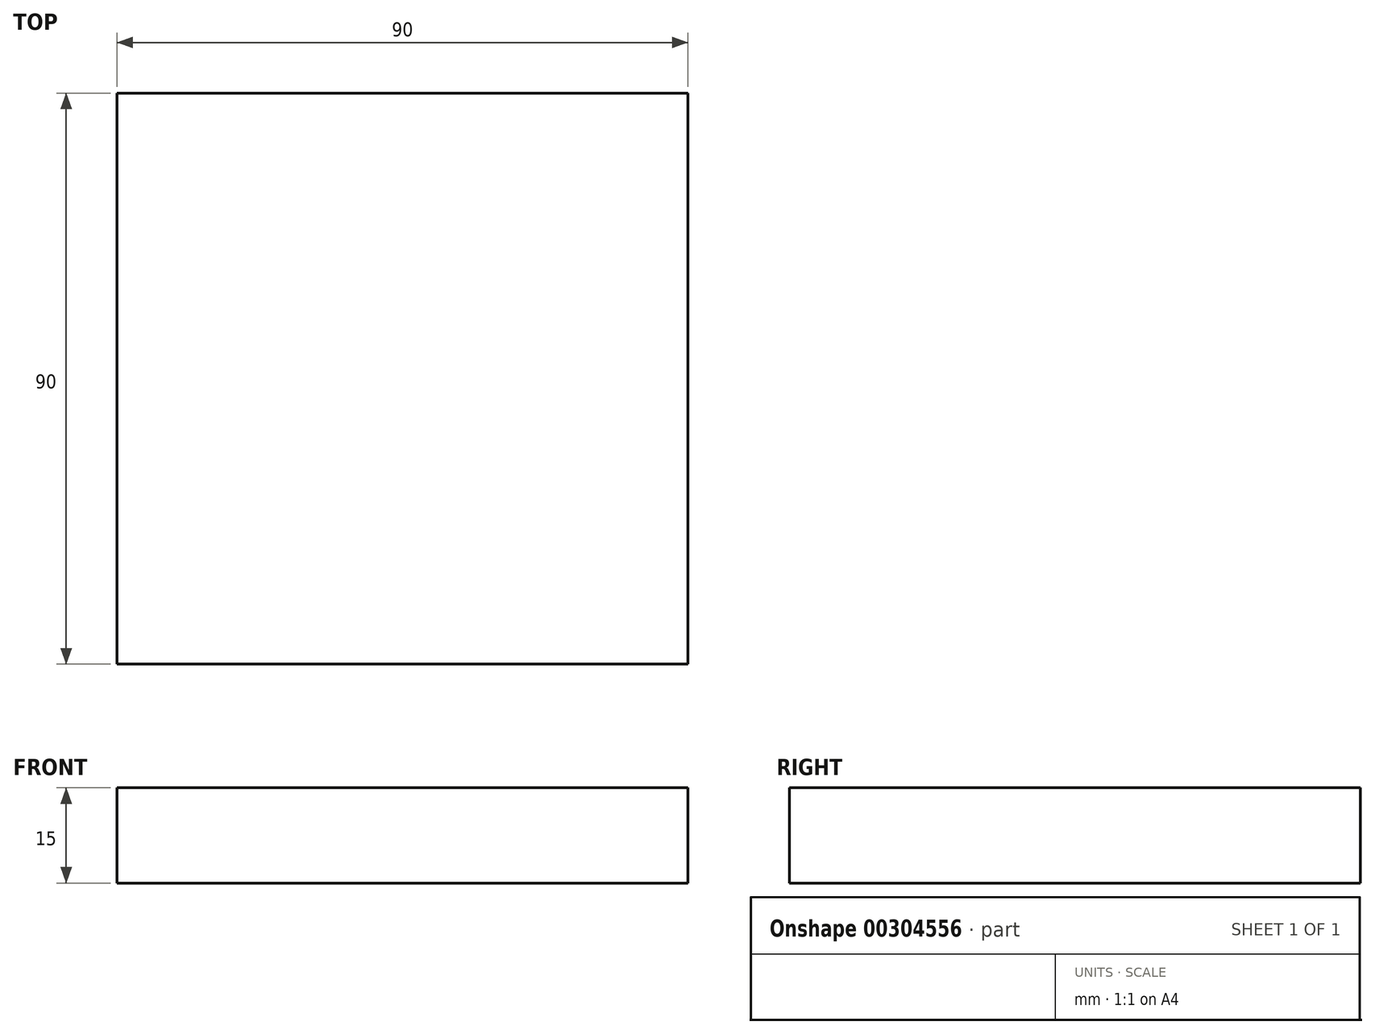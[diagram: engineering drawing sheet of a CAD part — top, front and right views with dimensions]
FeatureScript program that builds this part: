
annotation { "Feature Type Name" : "Feature", "Feature Type Description" : "" }
export const myFeature = defineFeature(function(context is Context, id is Id, definition is map)
    precondition{}
    {
        {
            var Q0;
            Q0=qCreatedBy(makeId("Top.planeOp"),FACE);
            var sketch = newSketch(context, id + "F0", { "sketchPlane" : qUnion([Q0])});
            skLineSegment(sketch, "E0.bottom", {"start": v(45, 45) * mm, "end": v(-45, 45) * mm});
            skLineSegment(sketch, "E0.top", {"start": v(45, -45) * mm, "end": v(-45, -45) * mm});
            skLineSegment(sketch, "E0.left", {"start": v(45, 45) * mm, "end": v(45, -45) * mm});
            skLineSegment(sketch, "E0.right", {"start": v(-45, 45) * mm, "end": v(-45, -45) * mm});
            skPoint(sketch, "E0.middle", {"position": v(0, 0) * mm});
            skSolve(sketch);
        }
        {
            var Q0;
            Q0 = qSketchRegion(id + "F0", true);
            extrude(context, id + "F1", {"entities" : qUnion([Q0]), "depth" : 15 * mm});
        }
    });
